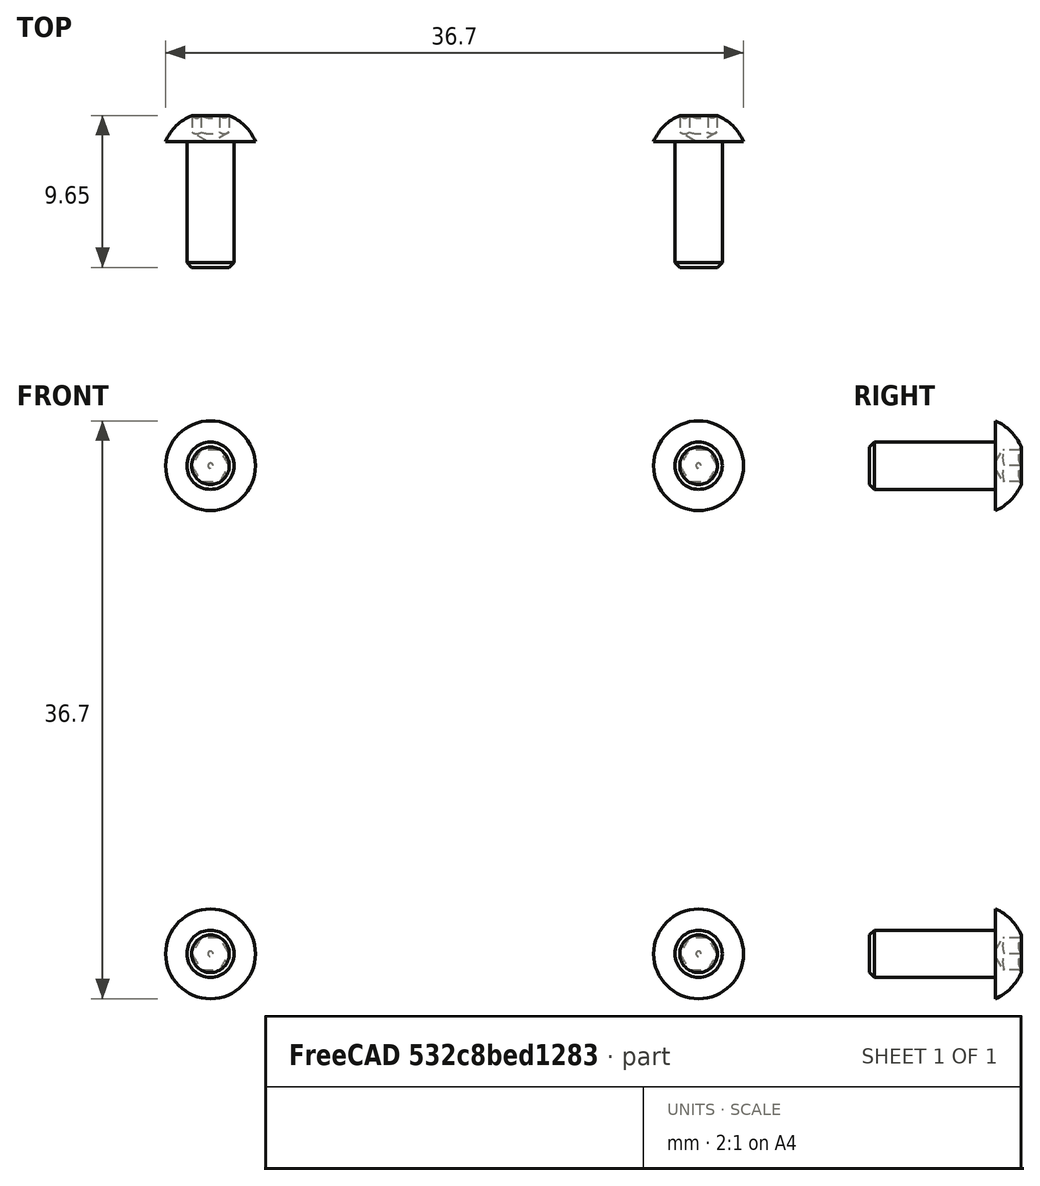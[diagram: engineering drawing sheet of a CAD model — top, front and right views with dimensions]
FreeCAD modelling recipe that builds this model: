
FCSTD DOCUMENT  (FreeCAD 0.20R29177 +426 (Git))
Label: ASM_DriveUnit
License: All rights reserved
LicenseURL: http://en.wikipedia.org/wiki/All_rights_reserved
objects: App::DocumentObjectGroup×4, Part::FeaturePython×4, App::Link×2, PartDesign::CoordinateSystem×1, App::FeaturePython×1, App::Part×1
note: 5 computed .brp shape members not serialized (recipe doc carries the construction recipe); baked Part::Feature solids carry a one-line shape summary decoded from their .brp
EXTERNAL_REF file=ASM_Stepper.FCStd obj=LCS_Origin
EXTERNAL_REF file=ASM_Stepper.FCStd obj=Assembly
EXTERNAL_REF file=ASM_DriveWheel.FCStd obj=LCS_Origin
EXTERNAL_REF file=ASM_Stepper.FCStd obj=Stepper_LCS_mount
EXTERNAL_REF file=ASM_DriveWheel.FCStd obj=Assembly
EXTERNAL_REF file=MotorBracket.FCStd obj=Body001
EXTERNAL_REF file=MotorBracket.FCStd obj=Mirrored001

FEATURE [App::DocumentObjectGroup] Parts
FEATURE [PartDesign::CoordinateSystem] LCS_Origin
  AttacherType = Attacher::AttachEngine3D
  MapMode = 2
  Support = -> [X_Axis]
FEATURE [App::FeaturePython] Variables  # WARN: FeaturePython — macro-defined, semantics opaque (R4)
  Type = App::PropertyContainer
FEATURE [App::DocumentObjectGroup] Constraints
FEATURE [App::DocumentObjectGroup] Configurations
FEATURE [App::Link] ASM_Stepper
  AttachedBy = #LCS_Origin
  AttachedTo = Parent Assembly#LCS_Origin
  LinkedObject = -> <external ASM_Stepper.FCStd>#Assembly
  SolverId = Asm4EE
  expr: Placement = LCS_Origin.Placement * AttachmentOffset * ASM_Stepper#LCS_Origin.Placement ^ -1
FEATURE [App::Link] ASM_DriveWheel
  AttachedBy = #LCS_Origin
  AttachedTo = ASM_Stepper#Stepper_LCS_mount
  AttachmentOffset = pos=(0,0,-14) rot=(0,0,1;0rad)
  LinkPlacement = pos=(0,11,30) rot=(1,0,0;1.5708rad)
  LinkedObject = -> <external ASM_DriveWheel.FCStd>#Assembly
  Placement = pos=(0,11,30) rot=(1,0,0;1.5708rad)
  SolverId = Asm4EE
  expr: Placement = ASM_Stepper.Placement * ASM_Stepper#Stepper_LCS_mount.Placement * AttachmentOffset * ASM_DriveWheel#LCS_Origin.Placement ^ -1
FEATURE [Part::FeaturePython] Screw  label="M3x8-Screw"  # Fasteners workbench fastener (typed FeaturePython)
  Placement = pos=(-15.5,-8.9e-14,45.5) rot=(-1,0,0;1.5708rad)
  baseObject = -> <external MotorBracket.FCStd>#Body001 [Edge90]
  diameter = 1
  invert = true
  leftHanded = false
  length = 1
  lengthCustom = 8
  matchOuter = true
  offset = 0
  thread = false
  type = 40
FEATURE [Part::FeaturePython] Screw001  label="M3x8-Screw007"  # Fasteners workbench fastener (typed FeaturePython)
  Placement = pos=(15.5,-7e-15,45.5) rot=(-1,0,0;1.5708rad)
  baseObject = -> <external MotorBracket.FCStd>#Mirrored001 [Edge87]
  diameter = 1
  invert = true
  leftHanded = false
  length = 1
  lengthCustom = 8
  matchOuter = true
  offset = 0
  thread = false
  type = 40
FEATURE [Part::FeaturePython] Screw002  label="M3x8-Screw008"  # Fasteners workbench fastener (typed FeaturePython)
  Placement = pos=(15.5,-7e-15,14.5) rot=(-1,0,0;1.5708rad)
  baseObject = -> <external MotorBracket.FCStd>#Mirrored001 [Edge88]
  diameter = 1
  invert = true
  leftHanded = false
  length = 1
  lengthCustom = 8
  matchOuter = true
  offset = 0
  thread = false
  type = 40
FEATURE [Part::FeaturePython] Screw003  label="M3x8-Screw009"  # Fasteners workbench fastener (typed FeaturePython)
  Placement = pos=(-15.5,-7e-15,14.5) rot=(-1,0,0;1.5708rad)
  baseObject = -> <external MotorBracket.FCStd>#Mirrored001 [Edge91]
  diameter = 1
  invert = true
  leftHanded = false
  length = 1
  lengthCustom = 8
  matchOuter = true
  offset = 0
  thread = false
  type = 40
FEATURE [App::DocumentObjectGroup] Fasteners
  Group = -> [Screw,Screw001,Screw002,Screw003]
FEATURE [App::Part] Assembly
  AssemblyType = Part::Link
  Group = -> [LCS_Origin,Variables,Constraints,Configurations,ASM_Stepper,ASM_DriveWheel,Fasteners,Screw,Screw001,Screw002,Screw003]
  Origin = -> Origin
  Type = Assembly

RESOLVED EXTERNAL PARTS (link-assembly join: the EXTERNAL_REF files above that resolve inside this repo's crawl, each included once):
---- part ASM_Stepper.FCStd = doc fcstd_b44b04883d39 ----
FCSTD DOCUMENT  (FreeCAD 0.20R29177 +426 (Git))
Label: ASM_Stepper
License: All rights reserved
LicenseURL: http://en.wikipedia.org/wiki/All_rights_reserved
objects: App::DocumentObjectGroup×3, PartDesign::CoordinateSystem×2, App::Link×2, App::FeaturePython×1, App::Part×1
note: 2 computed .brp shape members not serialized (recipe doc carries the construction recipe); baked Part::Feature solids carry a one-line shape summary decoded from their .brp
EXTERNAL_REF file=MotorBracket.FCStd obj=LCS_motor_mount
EXTERNAL_REF file=Stepper17.FCStd obj=LCS_mount
EXTERNAL_REF file=Stepper17.FCStd obj=Body
EXTERNAL_REF file=MotorBracket.FCStd obj=LCS_bottom
EXTERNAL_REF file=MotorBracket.FCStd obj=Assembly

FEATURE [App::DocumentObjectGroup] Parts
FEATURE [PartDesign::CoordinateSystem] LCS_Origin
  AttacherType = Attacher::AttachEngine3D
  MapMode = 2
  Support = -> [X_Axis]
FEATURE [App::FeaturePython] Variables  # WARN: FeaturePython — macro-defined, semantics opaque (R4)
  Type = App::PropertyContainer
FEATURE [App::DocumentObjectGroup] Constraints
FEATURE [App::DocumentObjectGroup] Configurations
FEATURE [App::Link] Stepper
  AssemblyType = Part::Link
  AttachedBy = #LCS_mount
  AttachedTo = MotorBracket#LCS_motor_mount
  LinkPlacement = pos=(0,-3,30) rot=(1,0,0;1.5708rad)
  LinkedObject = -> <external Stepper17.FCStd>#Body
  Placement = pos=(0,-3,30) rot=(1,0,0;1.5708rad)
  SolverId = Asm4EE
  expr: Placement = MotorBracket.Placement * MotorBracket#LCS_motor_mount.Placement * AttachmentOffset * Stepper17#LCS_mount.Placement ^ -1
FEATURE [App::Link] MotorBracket
  AttachedBy = #LCS_bottom
  AttachedTo = Parent Assembly#LCS_Origin
  LinkedObject = -> <external MotorBracket.FCStd>#Assembly
  SolverId = Asm4EE
  expr: Placement = LCS_Origin.Placement * AttachmentOffset * MotorBracket#LCS_bottom.Placement ^ -1
FEATURE [PartDesign::CoordinateSystem] Stepper_LCS_mount
  AttachedBy = Origin
  AttacherType = Attacher::AttachEngine3D
  Placement = pos=(0,-3,30) rot=(1,0,0;1.5708rad)
  SolverId = Asm4EE
  expr: Placement = Stepper.Placement * Stepper17#LCS_mount.Placement
FEATURE [App::Part] Assembly
  AssemblyType = Part::Link
  Group = -> [LCS_Origin,Variables,Constraints,Configurations,Stepper,MotorBracket,Stepper_LCS_mount]
  Origin = -> Origin
  Type = Assembly
---- part MotorBracket.FCStd = doc fcstd_48a7f3457e5c ----
FCSTD DOCUMENT  (FreeCAD 0.20R29177 +426 (Git))
Label: MotorBracket
License: All rights reserved
LicenseURL: http://en.wikipedia.org/wiki/All_rights_reserved
objects: Sketcher::SketchObject×5, PartDesign::Pocket×3, App::DocumentObjectGroup×3, PartDesign::Pad×2, PartDesign::Mirrored×2, PartDesign::CoordinateSystem×2, PartDesign::Plane×1, PartDesign::Body×1, App::FeaturePython×1, App::Part×1
note: 21 computed .brp shape members not serialized (recipe doc carries the construction recipe); baked Part::Feature solids carry a one-line shape summary decoded from their .brp

FEATURE [Sketcher::SketchObject] Sketch001
  FullyConstrained = true
  MapMode = 5
  Placement = pos=(0,0,0) rot=(0.57735,0.57735,0.57735;2.0944rad)
  Support = -> [YZ_Plane001]
  expr: Constraints[10] = <<Variables>>.SheetMetalThickness
  sketch-geometry (10):
    g0: LineSegment StartX=-3 StartY=4 StartZ=0 EndX=-3 EndY=51 EndZ=0
    g1: LineSegment StartX=-3 StartY=51 StartZ=0 EndX=0 EndY=51 EndZ=0
    g2: LineSegment StartX=0 StartY=51 StartZ=0 EndX=0 EndY=4 EndZ=0
    g3: LineSegment StartX=-4 StartY=0 StartZ=0 EndX=-51 EndY=0 EndZ=0
    g4: LineSegment StartX=-51 StartY=0 StartZ=0 EndX=-51 EndY=3 EndZ=0
    g5: LineSegment StartX=-51 StartY=3 StartZ=0 EndX=-4 EndY=3 EndZ=0
    g6: ArcOfCircle CenterX=-4 CenterY=4 CenterZ=0 NormalX=0 NormalY=0 NormalZ=1 AngleXU=0 Radius=1 StartAngle=4.71239 EndAngle=6.28319
    g7: GeomPoint X=-3 Y=3 Z=0
    g8: ArcOfCircle CenterX=-4 CenterY=4 CenterZ=0 NormalX=0 NormalY=0 NormalZ=1 AngleXU=0 Radius=4 StartAngle=4.71239 EndAngle=6.28319
    g9: GeomPoint X=0 Y=0 Z=0
  constraints (24):
    c: Coincident(g0,g1)
    c: Coincident(g1,g2)
    c: Horizontal(g1)
    c: Vertical(g0)
    c: Vertical(g2)
    c: Coincident(g3,g4)
    c: Coincident(g4,g5)
    c: Horizontal(g3)
    c: Horizontal(g5)
    c: Vertical(g4)
    c: DistanceX(g1,g1) = 3
    c: DistanceY(g9,g2) = 51
    c: Distance(g9,g3) = 51
    c: Coincident(g9,g-1)
    c: PointOnObject(g7,g0)
    c: PointOnObject(g7,g5)
    c: Tangent(g0,g6) = -1.5708
    c: Tangent(g5,g6) = -1.5708
    c: PointOnObject(g9,g2)
    c: PointOnObject(g9,g3)
    c: Tangent(g2,g8) = 1.5708
    c: Tangent(g3,g8) = 1.5708
    c: Radius(g6) = 1
    c: Coincident(g8,g6)
FEATURE [PartDesign::Pad] Pad001
  Direction = (1,-2e-16,3e-16)
  Length = 51
  Length2 = 25
  Midplane = true
  Placement = pos=(0,0,0) rot=(0.57735,0.57735,0.57735;2.0944rad)
  Profile = -> Sketch001
  ReferenceAxis = -> Sketch001 [N_Axis]
  Type = 0
FEATURE [Sketcher::SketchObject] Sketch002
  AttachmentOffset = pos=(0,30,0) rot=(0,0,1;0rad)
  FullyConstrained = true
  MapMode = 5
  Placement = pos=(0,-6.7e-15,30) rot=(1,0,0;1.5708rad)
  Support = -> [XZ_Plane001]
  sketch-geometry (10):
    g0: Circle CenterX=15.5 CenterY=15.5 CenterZ=0 NormalX=0 NormalY=0 NormalZ=1 AngleXU=0 Radius=1.6
    g1: LineSegment StartX=-15.5 StartY=15.5 StartZ=0 EndX=-15.5 EndY=-15.5 EndZ=0
    g2: LineSegment StartX=-15.5 StartY=-15.5 StartZ=0 EndX=15.5 EndY=-15.5 EndZ=0
    g3: LineSegment StartX=15.5 StartY=-15.5 StartZ=0 EndX=15.5 EndY=15.5 EndZ=0
    g4: LineSegment StartX=15.5 StartY=15.5 StartZ=0 EndX=-15.5 EndY=15.5 EndZ=0
    g5: GeomPoint X=0 Y=0 Z=0
    g6: Circle CenterX=0 CenterY=0 CenterZ=0 NormalX=0 NormalY=0 NormalZ=1 AngleXU=0 Radius=11
    g7: Circle CenterX=-15.5 CenterY=15.5 CenterZ=0 NormalX=0 NormalY=0 NormalZ=1 AngleXU=0 Radius=1.6
    g8: Circle CenterX=-15.5 CenterY=-15.5 CenterZ=0 NormalX=0 NormalY=0 NormalZ=1 AngleXU=0 Radius=1.6
    g9: Circle CenterX=15.5 CenterY=-15.5 CenterZ=0 NormalX=0 NormalY=0 NormalZ=1 AngleXU=0 Radius=1.6
  constraints (22):
    c: Diameter(g0) = 3.2
    c: Coincident(g1,g2)
    c: Coincident(g2,g3)
    c: Coincident(g3,g4)
    c: Coincident(g4,g1)
    c: Horizontal(g2)
    c: Horizontal(g4)
    c: Vertical(g1)
    c: Vertical(g3)
    c: Symmetric(g2,g1,g5)
    c: Equal(g3,g4)
    c: DistanceX(g4,g4) = 31
    c: Coincident(g0,g3)
    c: Coincident(g6,g5)
    c: Diameter(g6) = 22
    c: Coincident(g7,g1)
    c: Coincident(g8,g1)
    c: Coincident(g9,g2)
    c: Equal(g9,g8)
    c: Equal(g8,g7)
    c: Equal(g7,g0)
    c: Coincident(g6,g-1)
FEATURE [PartDesign::Pocket] Pocket001  label="MountHoles"
  BaseFeature = -> Pad001
  Direction = (0,1,2e-16)
  Length = 5
  Length2 = 100
  Placement = pos=(0,0,0) rot=(0.57735,0.57735,0.57735;2.0944rad)
  Profile = -> Sketch002
  Reversed = true
  Type = 1
FEATURE [Sketcher::SketchObject] Sketch003  label="SlotSketch"
  FullyConstrained = true
  MapMode = 5
  Support = -> [XY_Plane001]
  sketch-geometry (6):
    g0: LineSegment StartX=-15 StartY=0 StartZ=0 EndX=-15 EndY=-10.15 EndZ=0
    g1: ArcOfCircle CenterX=-15 CenterY=-10.15 CenterZ=0 NormalX=0 NormalY=0 NormalZ=1 AngleXU=0 Radius=2.15 StartAngle=-6.2e-15 EndAngle=3.1416
    g2: ArcOfCircle CenterX=-15 CenterY=-39.85 CenterZ=0 NormalX=0 NormalY=0 NormalZ=1 AngleXU=0 Radius=2.15 StartAngle=3.14159 EndAngle=6.28319
    g3: LineSegment StartX=-12.85 StartY=-10.15 StartZ=0 EndX=-12.85 EndY=-39.85 EndZ=0
    g4: LineSegment StartX=-17.15 StartY=-10.15 StartZ=0 EndX=-17.15 EndY=-39.85 EndZ=0
    g5: LineSegment StartX=-15 StartY=-39.85 StartZ=0 EndX=0 EndY=-39.85 EndZ=0
  constraints (17):
    c: PointOnObject(g0,g-1)
    c: Vertical(g0)
    c: DistanceY(g0,g0) = 10.15
    c: Coincident(g1,g0)
    c: Equal(g2,g1)
    c: Vertical(g3)
    c: Vertical(g4)
    c: Coincident(g5,g2)
    c: PointOnObject(g5,g-2)
    c: Horizontal(g5)
    c: Tangent(g1,g3) = 1.5708
    c: Coincident(g1,g4)
    c: Tangent(g2,g4) = -1.5708
    c: Tangent(g2,g3) = 1.5708
    c: DistanceX(g5,g5) = 15  'SlotOffsetX'
    c: Distance(g1,g1) = 4.3
    c: Distance(g1,g2) = 29.7
FEATURE [PartDesign::Pocket] Pocket002  label="BottomSlot"
  BaseFeature = -> Pocket001
  Direction = (0,0,-1)
  Length = 5
  Length2 = 100
  Placement = pos=(0,0,0) rot=(0.57735,0.57735,0.57735;2.0944rad)
  Profile = -> Sketch003
  Reversed = true
  Type = 1
FEATURE [Sketcher::SketchObject] Sketch
  AttachmentOffset = pos=(0,0,-25.5) rot=(0,0,1;0rad)
  FullyConstrained = true
  MapMode = 5
  Placement = pos=(-25.5,5.7e-15,-5.7e-15) rot=(0.57735,0.57735,0.57735;2.0944rad)
  Support = -> [YZ_Plane001]
  expr: .AttachmentOffset.Base.z = <<Pad001>>.Length / -2
  sketch-geometry (8):
    g0: LineSegment StartX=-3 StartY=23 StartZ=0 EndX=-23 EndY=3 EndZ=0
    g1: LineSegment StartX=-3 StartY=3 StartZ=0 EndX=-3 EndY=0 EndZ=0
    g2: LineSegment StartX=-3 StartY=0 StartZ=0 EndX=0 EndY=0 EndZ=0
    g3: LineSegment StartX=-3 StartY=3 StartZ=0 EndX=-3 EndY=5 EndZ=0
    g4: LineSegment StartX=-3 StartY=5 StartZ=0 EndX=-3 EndY=23 EndZ=0
    g5: LineSegment StartX=-23 StartY=3 StartZ=0 EndX=-5 EndY=3 EndZ=0
    g6: LineSegment StartX=-5 StartY=3 StartZ=0 EndX=-3 EndY=3 EndZ=0
    g7: LineSegment StartX=-5 StartY=3 StartZ=0 EndX=-3 EndY=5 EndZ=0
  constraints (22):
    c: Coincident(g0,g5)
    c: Coincident(g4,g0)
    c: DistanceY(g3,g4) = 20
    c: Coincident(g3,g6)
    c: DistanceY(g-1,g6) = 3
    c: Coincident(g1,g6)
    c: PointOnObject(g1,g-1)
    c: Coincident(g2,g1)
    c: Coincident(g2,g-1)
    c: Vertical(g1)
    c: Equal(g1,g2)
    c: Coincident(g3,g4)
    c: Vertical(g3)
    c: Vertical(g4)
    c: Coincident(g5,g6)
    c: Horizontal(g5)
    c: Horizontal(g6)
    c: Coincident(g7,g5)
    c: Coincident(g7,g4)
    c: Equal(g3,g6)
    c: DistanceX(g6,g6) = 2
    c: Equal(g4,g5)
FEATURE [PartDesign::Pad] Pad  label="Rib"
  BaseFeature = -> Pocket002
  Direction = (1,-2e-16,3e-16)
  Length = 3
  Length2 = 10
  Placement = pos=(0,0,0) rot=(0.57735,0.57735,0.57735;2.0944rad)
  Profile = -> Sketch
  ReferenceAxis = -> Sketch [N_Axis]
  Type = 0
  expr: Length = <<Variables>>.SheetMetalThickness
FEATURE [PartDesign::Mirrored] Mirrored
  BaseFeature = -> Pad
  MirrorPlane = -> YZ_Plane001
  Originals = -> [Pocket002,Pad]
  Placement = pos=(0,0,0) rot=(0.57735,0.57735,0.57735;2.0944rad)
FEATURE [Sketcher::SketchObject] Sketch004
  FullyConstrained = true
  MapMode = 5
  Placement = pos=(0,0,0) rot=(1,0,0;1.5708rad)
  Support = -> [XZ_Plane001]
  sketch-geometry (6):
    g0: LineSegment StartX=-72.5 StartY=0 StartZ=0 EndX=0 EndY=72.5 EndZ=0
    g1: LineSegment StartX=0 StartY=72.5 StartZ=0 EndX=72.5 EndY=0 EndZ=0
    g2: LineSegment StartX=72.5 StartY=0 StartZ=0 EndX=72.5 EndY=145 EndZ=0
    g3: LineSegment StartX=-72.5 StartY=0 StartZ=0 EndX=-72.5 EndY=145 EndZ=0
    g4: LineSegment StartX=-72.5 StartY=145 StartZ=0 EndX=72.5 EndY=145 EndZ=0
    g5: LineSegment StartX=-21.5 StartY=51 StartZ=0 EndX=21.5 EndY=51 EndZ=0
  constraints (19):
    c: PointOnObject(g0,g-1)
    c: PointOnObject(g0,g-2)
    c: Coincident(g1,g0)
    c: PointOnObject(g1,g-1)
    c: Coincident(g2,g1)
    c: Vertical(g2)
    c: Coincident(g3,g0)
    c: Vertical(g3)
    c: Coincident(g4,g3)
    c: Coincident(g4,g2)
    c: Horizontal(g4)
    c: Equal(g1,g0)
    c: Angle(g1,g-1) = 0.785398
    c: Equal(g2,g4)
    c: PointOnObject(g5,g0)
    c: PointOnObject(g5,g1)
    c: Horizontal(g5)
    c: DistanceY(g-1,g5) = 51
    c: DistanceX(g5,g5) = 43
FEATURE [PartDesign::Pocket] Pocket  label="CornerChamfer"
  BaseFeature = -> Mirrored
  Direction = (0,1,2e-16)
  Length = 5
  Length2 = 5
  Placement = pos=(0,0,0) rot=(0.57735,0.57735,0.57735;2.0944rad)
  Profile = -> Sketch004
  ReferenceAxis = -> Sketch004 [N_Axis]
  Reversed = true
  Type = 1
FEATURE [PartDesign::Plane] DatumPlane  label="ChamferMirrorRef"
  AttachmentOffset = pos=(0,0,0) rot=(1,0,0;0.785398rad)
  Length = 65.8074
  MapMode = 5
  Placement = pos=(0,0,0) rot=(1,0,0;2.35619rad)
  ResizeMode = 0
  Support = -> [XZ_Plane001]
  Width = 122.288
FEATURE [PartDesign::Mirrored] Mirrored001  label="ChamferMirror"
  BaseFeature = -> Pocket
  MirrorPlane = -> DatumPlane
  Originals = -> [Pocket]
  Placement = pos=(0,0,0) rot=(0.57735,0.57735,0.57735;2.0944rad)
FEATURE [PartDesign::Body] Body001
  Group = -> [Sketch001,Pad001,Sketch002,Pocket001,Sketch003,Pocket002,Sketch,Pad,Mirrored,Sketch004,Pocket,DatumPlane,Mirrored001]
  Origin = -> Origin001
  Tip = -> Mirrored001
FEATURE [App::DocumentObjectGroup] Parts
FEATURE [App::FeaturePython] Variables  # WARN: FeaturePython — macro-defined, semantics opaque (R4)
  SheetMetalThickness = 3
  Type = App::PropertyContainer
FEATURE [App::DocumentObjectGroup] Constraints
FEATURE [App::DocumentObjectGroup] Configurations
FEATURE [PartDesign::CoordinateSystem] LCS_bottom
  AttacherType = Attacher::AttachEngine3D
  MapMode = 2
  Support = -> [XY_Plane]
FEATURE [PartDesign::CoordinateSystem] LCS_motor_mount
  AttacherType = Attacher::AttachEngine3D
  AttachmentOffset = pos=(0,0,3) rot=(0,0,1;0rad)
  MapMode = 2
  Placement = pos=(0,-3,30) rot=(1,0,0;1.5708rad)
  Support = -> [Sketch002]
  expr: .AttachmentOffset.Base.z = <<Variables>>.SheetMetalThickness
FEATURE [App::Part] Assembly
  AssemblyType = Part::Link
  Group = -> [Variables,Constraints,Configurations,Body001,LCS_bottom,LCS_motor_mount]
  Origin = -> Origin
  Type = Assembly
